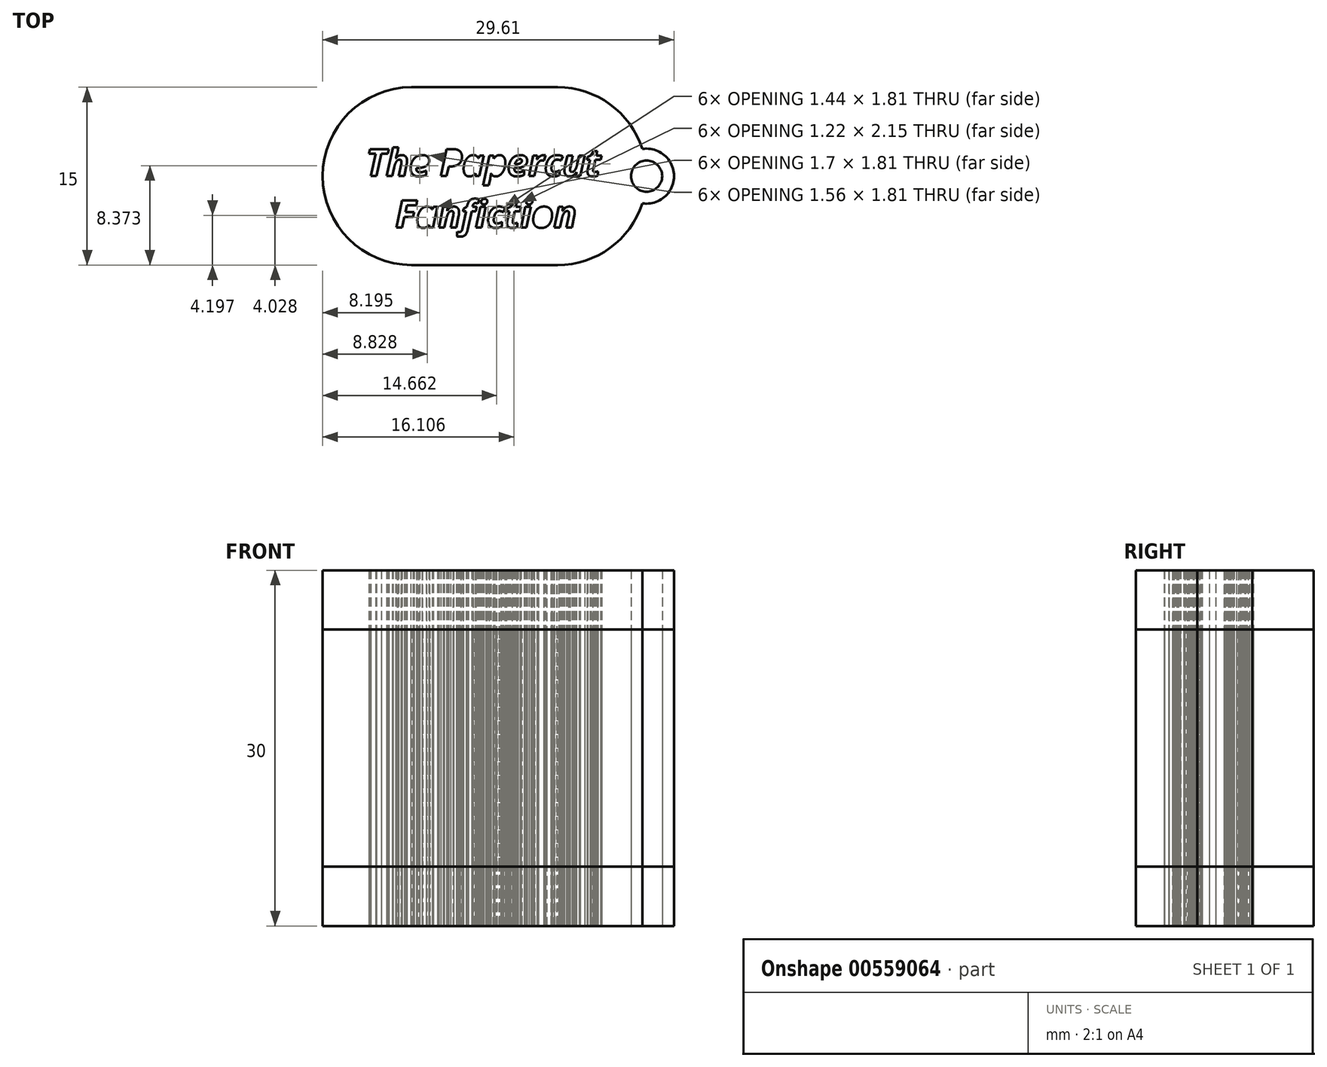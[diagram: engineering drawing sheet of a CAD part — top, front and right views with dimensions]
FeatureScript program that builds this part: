
annotation { "Feature Type Name" : "Feature", "Feature Type Description" : "" }
export const myFeature = defineFeature(function(context is Context, id is Id, definition is map)
    precondition{}
    {
        {
            var Q0;
            Q0=qCreatedBy(makeId("Top.planeOp"),FACE);
            var sketch = newSketch(context, id + "F0", { "sketchPlane" : qUnion([Q0])});
            skText(sketch, "E0", { "text": "The Papercut\n   Fanfiction", "fontName": "OpenSans-BoldItalic.ttf"});
            skLineSegment(sketch, "E1.bottom", {"start": v(6.15, 7.5) * mm, "end": v(-6.15, 7.5) * mm});
            skLineSegment(sketch, "E1.top", {"start": v(6.15, -7.5) * mm, "end": v(-6.15, -7.5) * mm});
            skLineSegment(sketch, "E1.left", {"start": v(13.65, 0) * mm, "end": v(13.65, 0) * mm});
            skLineSegment(sketch, "E1.right", {"start": v(-13.65, 0) * mm, "end": v(-13.65, 0) * mm});
            skPoint(sketch, "E1.middle", {"position": v(0, 0) * mm});
            skPoint(sketch, "E2.visualSharp", {"position": v(-13.65, 7.5) * mm});
            skArc(sketch, "E2.filletArc", {"start": v(-6.15, 7.5) * mm, "mid": v(-11.45, 5.3) * mm, "end": v(-13.65, 0) * mm});
            skPoint(sketch, "E3.visualSharp", {"position": v(-13.65, -7.5) * mm});
            skArc(sketch, "E3.filletArc", {"start": v(-13.65, 0) * mm, "mid": v(-11.45, -5.3) * mm, "end": v(-6.15, -7.5) * mm});
            skPoint(sketch, "E4.visualSharp", {"position": v(13.65, 7.5) * mm});
            skPoint(sketch, "E5.visualSharp", {"position": v(13.65, -7.5) * mm});
            skArc(sketch, "E5.filletArc", {"start": v(6.15, -7.5) * mm, "mid": v(10.57, -6.06) * mm, "end": v(13.3, -2.3) * mm});
            skLineSegment(sketch, "E6", {"start": v(13.65, 0) * mm, "end": v(13.64, 0) * mm, "construction": true});
            skArc(sketch, "E7", {"start": v(13.3, -2.3) * mm, "mid": v(15.96, 0) * mm, "end": v(13.3, 2.3) * mm});
            skPoint(sketch, "E8.end.orphan", {"position": v(12.47, 0) * mm});
            skCircle(sketch, "E9", {"center": v(13.65, 0) * mm, "radius": 1.31 * mm});
            skArc(sketch, "E10.trimOffspring", {"start": v(13.3, 2.3) * mm, "mid": v(10.57, 6.06) * mm, "end": v(6.15, 7.5) * mm});
            const initialGuessF0  = {"E0": [-0.01, 0, 1, 0, 0.0023]};
            skSetInitialGuess(sketch, initialGuessF0);
            skSolve(sketch);
        }
        {
            var Q0;
            Q0=makeQuery(id+"F0.imprint","IMPRINT",FACE,{"disambiguationData":[TD([[makeQuery(id+"F0.imprint","IMPRINT",EDGE,{"derivedFrom":sQuery(id+"F0.wireOp",EDGE,"E0.sketch_text.stroke-0")}),1.0]])]});
            extrude(context, id + "F1", {"entities" : qUnion([Q0]), "depth" : 5 * mm, "offsetDistance" : 25 * mm});
        }
        {
            var Q0;
            Q0=makeQuery(id+"F1.opExtrude","CAP_FACE",FACE,{"disambiguationData":[OSD([sQuery(id+"F0.wireOp",EDGE,"E0.sketch_text.stroke-0"),sQuery(id+"F0.wireOp",EDGE,"E0.sketch_text.stroke-1"),sQuery(id+"F0.wireOp",EDGE,"E0.sketch_text.stroke-2"),sQuery(id+"F0.wireOp",EDGE,"E0.sketch_text.stroke-3"),sQuery(id+"F0.wireOp",EDGE,"E0.sketch_text.stroke-4"),sQuery(id+"F0.wireOp",EDGE,"E0.sketch_text.stroke-5"),sQuery(id+"F0.wireOp",EDGE,"E0.sketch_text.stroke-6"),sQuery(id+"F0.wireOp",EDGE,"E0.sketch_text.stroke-7"),sQuery(id+"F0.wireOp",EDGE,"E0.sketch_text.stroke-8"),sQuery(id+"F0.wireOp",EDGE,"E0.sketch_text.stroke-9"),sQuery(id+"F0.wireOp",EDGE,"E0.sketch_text.stroke-10"),sQuery(id+"F0.wireOp",EDGE,"E0.sketch_text.stroke-11"),sQuery(id+"F0.wireOp",EDGE,"E0.sketch_text.stroke-12"),sQuery(id+"F0.wireOp",EDGE,"E0.sketch_text.stroke-13"),sQuery(id+"F0.wireOp",EDGE,"E0.sketch_text.stroke-14"),sQuery(id+"F0.wireOp",EDGE,"E0.sketch_text.stroke-15"),sQuery(id+"F0.wireOp",EDGE,"E0.sketch_text.stroke-16"),sQuery(id+"F0.wireOp",EDGE,"E0.sketch_text.stroke-17"),sQuery(id+"F0.wireOp",EDGE,"E0.sketch_text.stroke-18"),sQuery(id+"F0.wireOp",EDGE,"E0.sketch_text.stroke-19"),sQuery(id+"F0.wireOp",EDGE,"E0.sketch_text.stroke-20"),sQuery(id+"F0.wireOp",EDGE,"E0.sketch_text.stroke-21"),sQuery(id+"F0.wireOp",EDGE,"E0.sketch_text.stroke-22"),sQuery(id+"F0.wireOp",EDGE,"E0.sketch_text.stroke-23"),sQuery(id+"F0.wireOp",EDGE,"E0.sketch_text.stroke-24"),sQuery(id+"F0.wireOp",EDGE,"E0.sketch_text.stroke-25"),sQuery(id+"F0.wireOp",EDGE,"E0.sketch_text.stroke-26"),sQuery(id+"F0.wireOp",EDGE,"E0.sketch_text.stroke-33"),sQuery(id+"F0.wireOp",EDGE,"E0.sketch_text.stroke-34"),sQuery(id+"F0.wireOp",EDGE,"E0.sketch_text.stroke-35"),sQuery(id+"F0.wireOp",EDGE,"E0.sketch_text.stroke-36"),sQuery(id+"F0.wireOp",EDGE,"E0.sketch_text.stroke-37"),sQuery(id+"F0.wireOp",EDGE,"E0.sketch_text.stroke-38"),sQuery(id+"F0.wireOp",EDGE,"E0.sketch_text.stroke-39"),sQuery(id+"F0.wireOp",EDGE,"E0.sketch_text.stroke-40"),sQuery(id+"F0.wireOp",EDGE,"E0.sketch_text.stroke-41"),sQuery(id+"F0.wireOp",EDGE,"E0.sketch_text.stroke-42"),sQuery(id+"F0.wireOp",EDGE,"E0.sketch_text.stroke-43"),sQuery(id+"F0.wireOp",EDGE,"E0.sketch_text.stroke-44"),sQuery(id+"F0.wireOp",EDGE,"E0.sketch_text.stroke-45"),sQuery(id+"F0.wireOp",EDGE,"E0.sketch_text.stroke-46"),sQuery(id+"F0.wireOp",EDGE,"E0.sketch_text.stroke-47"),sQuery(id+"F0.wireOp",EDGE,"E0.sketch_text.stroke-48"),sQuery(id+"F0.wireOp",EDGE,"E0.sketch_text.stroke-49"),sQuery(id+"F0.wireOp",EDGE,"E0.sketch_text.stroke-50"),sQuery(id+"F0.wireOp",EDGE,"E0.sketch_text.stroke-57"),sQuery(id+"F0.wireOp",EDGE,"E0.sketch_text.stroke-58"),sQuery(id+"F0.wireOp",EDGE,"E0.sketch_text.stroke-59"),sQuery(id+"F0.wireOp",EDGE,"E0.sketch_text.stroke-60"),sQuery(id+"F0.wireOp",EDGE,"E0.sketch_text.stroke-61"),sQuery(id+"F0.wireOp",EDGE,"E0.sketch_text.stroke-62"),sQuery(id+"F0.wireOp",EDGE,"E0.sketch_text.stroke-63"),sQuery(id+"F0.wireOp",EDGE,"E0.sketch_text.stroke-64"),sQuery(id+"F0.wireOp",EDGE,"E0.sketch_text.stroke-65"),sQuery(id+"F0.wireOp",EDGE,"E0.sketch_text.stroke-66"),sQuery(id+"F0.wireOp",EDGE,"E0.sketch_text.stroke-67"),sQuery(id+"F0.wireOp",EDGE,"E0.sketch_text.stroke-68"),sQuery(id+"F0.wireOp",EDGE,"E0.sketch_text.stroke-69"),sQuery(id+"F0.wireOp",EDGE,"E0.sketch_text.stroke-70"),sQuery(id+"F0.wireOp",EDGE,"E0.sketch_text.stroke-71"),sQuery(id+"F0.wireOp",EDGE,"E0.sketch_text.stroke-72"),sQuery(id+"F0.wireOp",EDGE,"E0.sketch_text.stroke-73"),sQuery(id+"F0.wireOp",EDGE,"E0.sketch_text.stroke-74"),sQuery(id+"F0.wireOp",EDGE,"E0.sketch_text.stroke-75"),sQuery(id+"F0.wireOp",EDGE,"E0.sketch_text.stroke-76"),sQuery(id+"F0.wireOp",EDGE,"E0.sketch_text.stroke-77"),sQuery(id+"F0.wireOp",EDGE,"E0.sketch_text.stroke-78"),sQuery(id+"F0.wireOp",EDGE,"E0.sketch_text.stroke-79"),sQuery(id+"F0.wireOp",EDGE,"E0.sketch_text.stroke-80"),sQuery(id+"F0.wireOp",EDGE,"E0.sketch_text.stroke-91"),sQuery(id+"F0.wireOp",EDGE,"E0.sketch_text.stroke-92"),sQuery(id+"F0.wireOp",EDGE,"E0.sketch_text.stroke-93"),sQuery(id+"F0.wireOp",EDGE,"E0.sketch_text.stroke-94"),sQuery(id+"F0.wireOp",EDGE,"E0.sketch_text.stroke-95"),sQuery(id+"F0.wireOp",EDGE,"E0.sketch_text.stroke-96"),sQuery(id+"F0.wireOp",EDGE,"E0.sketch_text.stroke-97"),sQuery(id+"F0.wireOp",EDGE,"E0.sketch_text.stroke-98"),sQuery(id+"F0.wireOp",EDGE,"E0.sketch_text.stroke-99"),sQuery(id+"F0.wireOp",EDGE,"E0.sketch_text.stroke-100"),sQuery(id+"F0.wireOp",EDGE,"E0.sketch_text.stroke-101"),sQuery(id+"F0.wireOp",EDGE,"E0.sketch_text.stroke-102"),sQuery(id+"F0.wireOp",EDGE,"E0.sketch_text.stroke-103"),sQuery(id+"F0.wireOp",EDGE,"E0.sketch_text.stroke-104"),sQuery(id+"F0.wireOp",EDGE,"E0.sketch_text.stroke-105"),sQuery(id+"F0.wireOp",EDGE,"E0.sketch_text.stroke-106"),sQuery(id+"F0.wireOp",EDGE,"E0.sketch_text.stroke-122"),sQuery(id+"F0.wireOp",EDGE,"E0.sketch_text.stroke-123"),sQuery(id+"F0.wireOp",EDGE,"E0.sketch_text.stroke-124"),sQuery(id+"F0.wireOp",EDGE,"E0.sketch_text.stroke-125"),sQuery(id+"F0.wireOp",EDGE,"E0.sketch_text.stroke-126"),sQuery(id+"F0.wireOp",EDGE,"E0.sketch_text.stroke-127"),sQuery(id+"F0.wireOp",EDGE,"E0.sketch_text.stroke-128"),sQuery(id+"F0.wireOp",EDGE,"E0.sketch_text.stroke-129"),sQuery(id+"F0.wireOp",EDGE,"E0.sketch_text.stroke-130"),sQuery(id+"F0.wireOp",EDGE,"E0.sketch_text.stroke-131"),sQuery(id+"F0.wireOp",EDGE,"E0.sketch_text.stroke-132"),sQuery(id+"F0.wireOp",EDGE,"E0.sketch_text.stroke-133"),sQuery(id+"F0.wireOp",EDGE,"E0.sketch_text.stroke-134"),sQuery(id+"F0.wireOp",EDGE,"E0.sketch_text.stroke-135"),sQuery(id+"F0.wireOp",EDGE,"E0.sketch_text.stroke-136"),sQuery(id+"F0.wireOp",EDGE,"E0.sketch_text.stroke-137"),sQuery(id+"F0.wireOp",EDGE,"E0.sketch_text.stroke-138"),sQuery(id+"F0.wireOp",EDGE,"E0.sketch_text.stroke-139"),sQuery(id+"F0.wireOp",EDGE,"E0.sketch_text.stroke-140"),sQuery(id+"F0.wireOp",EDGE,"E0.sketch_text.stroke-141"),sQuery(id+"F0.wireOp",EDGE,"E0.sketch_text.stroke-142"),sQuery(id+"F0.wireOp",EDGE,"E0.sketch_text.stroke-143"),sQuery(id+"F0.wireOp",EDGE,"E0.sketch_text.stroke-144"),sQuery(id+"F0.wireOp",EDGE,"E0.sketch_text.stroke-145"),sQuery(id+"F0.wireOp",EDGE,"E0.sketch_text.stroke-146"),sQuery(id+"F0.wireOp",EDGE,"E0.sketch_text.stroke-147"),sQuery(id+"F0.wireOp",EDGE,"E0.sketch_text.stroke-148"),sQuery(id+"F0.wireOp",EDGE,"E0.sketch_text.stroke-149"),sQuery(id+"F0.wireOp",EDGE,"E0.sketch_text.stroke-150"),sQuery(id+"F0.wireOp",EDGE,"E0.sketch_text.stroke-151"),sQuery(id+"F0.wireOp",EDGE,"E0.sketch_text.stroke-152"),sQuery(id+"F0.wireOp",EDGE,"E0.sketch_text.stroke-153"),sQuery(id+"F0.wireOp",EDGE,"E0.sketch_text.stroke-154"),sQuery(id+"F0.wireOp",EDGE,"E0.sketch_text.stroke-155"),sQuery(id+"F0.wireOp",EDGE,"E0.sketch_text.stroke-156"),sQuery(id+"F0.wireOp",EDGE,"E0.sketch_text.stroke-157"),sQuery(id+"F0.wireOp",EDGE,"E0.sketch_text.stroke-158"),sQuery(id+"F0.wireOp",EDGE,"E0.sketch_text.stroke-159"),sQuery(id+"F0.wireOp",EDGE,"E0.sketch_text.stroke-160"),sQuery(id+"F0.wireOp",EDGE,"E0.sketch_text.stroke-161"),sQuery(id+"F0.wireOp",EDGE,"E0.sketch_text.stroke-162"),sQuery(id+"F0.wireOp",EDGE,"E0.sketch_text.stroke-163"),sQuery(id+"F0.wireOp",EDGE,"E0.sketch_text.stroke-164"),sQuery(id+"F0.wireOp",EDGE,"E0.sketch_text.stroke-165"),sQuery(id+"F0.wireOp",EDGE,"E0.sketch_text.stroke-166"),sQuery(id+"F0.wireOp",EDGE,"E0.sketch_text.stroke-167"),sQuery(id+"F0.wireOp",EDGE,"E0.sketch_text.stroke-168"),sQuery(id+"F0.wireOp",EDGE,"E0.sketch_text.stroke-169"),sQuery(id+"F0.wireOp",EDGE,"E0.sketch_text.stroke-170"),sQuery(id+"F0.wireOp",EDGE,"E0.sketch_text.stroke-171"),sQuery(id+"F0.wireOp",EDGE,"E0.sketch_text.stroke-172"),sQuery(id+"F0.wireOp",EDGE,"E0.sketch_text.stroke-173"),sQuery(id+"F0.wireOp",EDGE,"E0.sketch_text.stroke-174"),sQuery(id+"F0.wireOp",EDGE,"E0.sketch_text.stroke-175"),sQuery(id+"F0.wireOp",EDGE,"E0.sketch_text.stroke-176"),sQuery(id+"F0.wireOp",EDGE,"E0.sketch_text.stroke-177"),sQuery(id+"F0.wireOp",EDGE,"E0.sketch_text.stroke-178"),sQuery(id+"F0.wireOp",EDGE,"E0.sketch_text.stroke-179"),sQuery(id+"F0.wireOp",EDGE,"E0.sketch_text.stroke-180"),sQuery(id+"F0.wireOp",EDGE,"E0.sketch_text.stroke-181"),sQuery(id+"F0.wireOp",EDGE,"E0.sketch_text.stroke-182"),sQuery(id+"F0.wireOp",EDGE,"E0.sketch_text.stroke-183"),sQuery(id+"F0.wireOp",EDGE,"E0.sketch_text.stroke-184"),sQuery(id+"F0.wireOp",EDGE,"E0.sketch_text.stroke-185"),sQuery(id+"F0.wireOp",EDGE,"E0.sketch_text.stroke-186"),sQuery(id+"F0.wireOp",EDGE,"E0.sketch_text.stroke-187"),sQuery(id+"F0.wireOp",EDGE,"E0.sketch_text.stroke-188"),sQuery(id+"F0.wireOp",EDGE,"E0.sketch_text.stroke-189"),sQuery(id+"F0.wireOp",EDGE,"E0.sketch_text.stroke-190"),sQuery(id+"F0.wireOp",EDGE,"E0.sketch_text.stroke-191"),sQuery(id+"F0.wireOp",EDGE,"E0.sketch_text.stroke-192"),sQuery(id+"F0.wireOp",EDGE,"E0.sketch_text.stroke-193"),sQuery(id+"F0.wireOp",EDGE,"E0.sketch_text.stroke-194"),sQuery(id+"F0.wireOp",EDGE,"E0.sketch_text.stroke-195"),sQuery(id+"F0.wireOp",EDGE,"E0.sketch_text.stroke-196"),sQuery(id+"F0.wireOp",EDGE,"E0.sketch_text.stroke-197"),sQuery(id+"F0.wireOp",EDGE,"E0.sketch_text.stroke-198"),sQuery(id+"F0.wireOp",EDGE,"E0.sketch_text.stroke-199"),sQuery(id+"F0.wireOp",EDGE,"E0.sketch_text.stroke-200"),sQuery(id+"F0.wireOp",EDGE,"E0.sketch_text.stroke-201"),sQuery(id+"F0.wireOp",EDGE,"E0.sketch_text.stroke-202"),sQuery(id+"F0.wireOp",EDGE,"E0.sketch_text.stroke-203"),sQuery(id+"F0.wireOp",EDGE,"E0.sketch_text.stroke-204"),sQuery(id+"F0.wireOp",EDGE,"E0.sketch_text.stroke-205"),sQuery(id+"F0.wireOp",EDGE,"E0.sketch_text.stroke-206"),sQuery(id+"F0.wireOp",EDGE,"E0.sketch_text.stroke-207"),sQuery(id+"F0.wireOp",EDGE,"E0.sketch_text.stroke-208"),sQuery(id+"F0.wireOp",EDGE,"E0.sketch_text.stroke-209"),sQuery(id+"F0.wireOp",EDGE,"E0.sketch_text.stroke-210"),sQuery(id+"F0.wireOp",EDGE,"E0.sketch_text.stroke-211"),sQuery(id+"F0.wireOp",EDGE,"E0.sketch_text.stroke-212"),sQuery(id+"F0.wireOp",EDGE,"E0.sketch_text.stroke-213"),sQuery(id+"F0.wireOp",EDGE,"E0.sketch_text.stroke-214"),sQuery(id+"F0.wireOp",EDGE,"E0.sketch_text.stroke-215"),sQuery(id+"F0.wireOp",EDGE,"E0.sketch_text.stroke-216"),sQuery(id+"F0.wireOp",EDGE,"E0.sketch_text.stroke-217"),sQuery(id+"F0.wireOp",EDGE,"E0.sketch_text.stroke-218"),sQuery(id+"F0.wireOp",EDGE,"E0.sketch_text.stroke-219"),sQuery(id+"F0.wireOp",EDGE,"E0.sketch_text.stroke-220"),sQuery(id+"F0.wireOp",EDGE,"E0.sketch_text.stroke-221"),sQuery(id+"F0.wireOp",EDGE,"E0.sketch_text.stroke-222"),sQuery(id+"F0.wireOp",EDGE,"E0.sketch_text.stroke-223"),sQuery(id+"F0.wireOp",EDGE,"E0.sketch_text.stroke-224"),sQuery(id+"F0.wireOp",EDGE,"E0.sketch_text.stroke-225"),sQuery(id+"F0.wireOp",EDGE,"E0.sketch_text.stroke-226"),sQuery(id+"F0.wireOp",EDGE,"E0.sketch_text.stroke-227"),sQuery(id+"F0.wireOp",EDGE,"E0.sketch_text.stroke-228"),sQuery(id+"F0.wireOp",EDGE,"E0.sketch_text.stroke-229"),sQuery(id+"F0.wireOp",EDGE,"E0.sketch_text.stroke-230"),sQuery(id+"F0.wireOp",EDGE,"E0.sketch_text.stroke-241"),sQuery(id+"F0.wireOp",EDGE,"E0.sketch_text.stroke-242"),sQuery(id+"F0.wireOp",EDGE,"E0.sketch_text.stroke-243"),sQuery(id+"F0.wireOp",EDGE,"E0.sketch_text.stroke-244"),sQuery(id+"F0.wireOp",EDGE,"E0.sketch_text.stroke-245"),sQuery(id+"F0.wireOp",EDGE,"E0.sketch_text.stroke-246"),sQuery(id+"F0.wireOp",EDGE,"E0.sketch_text.stroke-247"),sQuery(id+"F0.wireOp",EDGE,"E0.sketch_text.stroke-248"),sQuery(id+"F0.wireOp",EDGE,"E0.sketch_text.stroke-249"),sQuery(id+"F0.wireOp",EDGE,"E0.sketch_text.stroke-250"),sQuery(id+"F0.wireOp",EDGE,"E0.sketch_text.stroke-251"),sQuery(id+"F0.wireOp",EDGE,"E0.sketch_text.stroke-252"),sQuery(id+"F0.wireOp",EDGE,"E0.sketch_text.stroke-253"),sQuery(id+"F0.wireOp",EDGE,"E0.sketch_text.stroke-254"),sQuery(id+"F0.wireOp",EDGE,"E0.sketch_text.stroke-255"),sQuery(id+"F0.wireOp",EDGE,"E0.sketch_text.stroke-256"),sQuery(id+"F0.wireOp",EDGE,"E0.sketch_text.stroke-257"),sQuery(id+"F0.wireOp",EDGE,"E0.sketch_text.stroke-258"),sQuery(id+"F0.wireOp",EDGE,"E0.sketch_text.stroke-259"),sQuery(id+"F0.wireOp",EDGE,"E0.sketch_text.stroke-260"),sQuery(id+"F0.wireOp",EDGE,"E0.sketch_text.stroke-261"),sQuery(id+"F0.wireOp",EDGE,"E0.sketch_text.stroke-262"),sQuery(id+"F0.wireOp",EDGE,"E0.sketch_text.stroke-263"),sQuery(id+"F0.wireOp",EDGE,"E0.sketch_text.stroke-264"),sQuery(id+"F0.wireOp",EDGE,"E0.sketch_text.stroke-265"),sQuery(id+"F0.wireOp",EDGE,"E0.sketch_text.stroke-266"),sQuery(id+"F0.wireOp",EDGE,"E0.sketch_text.stroke-267"),sQuery(id+"F0.wireOp",EDGE,"E0.sketch_text.stroke-268"),sQuery(id+"F0.wireOp",EDGE,"E0.sketch_text.stroke-269"),sQuery(id+"F0.wireOp",EDGE,"E0.sketch_text.stroke-270"),sQuery(id+"F0.wireOp",EDGE,"E0.sketch_text.stroke-271"),sQuery(id+"F0.wireOp",EDGE,"E0.sketch_text.stroke-272"),sQuery(id+"F0.wireOp",EDGE,"E0.sketch_text.stroke-273"),sQuery(id+"F0.wireOp",EDGE,"E0.sketch_text.stroke-274"),sQuery(id+"F0.wireOp",EDGE,"E0.sketch_text.stroke-275"),sQuery(id+"F0.wireOp",EDGE,"E0.sketch_text.stroke-276"),sQuery(id+"F0.wireOp",EDGE,"E0.sketch_text.stroke-277"),sQuery(id+"F0.wireOp",EDGE,"E0.sketch_text.stroke-278"),sQuery(id+"F0.wireOp",EDGE,"E0.sketch_text.stroke-279"),sQuery(id+"F0.wireOp",EDGE,"E0.sketch_text.stroke-280"),sQuery(id+"F0.wireOp",EDGE,"E0.sketch_text.stroke-281"),sQuery(id+"F0.wireOp",EDGE,"E0.sketch_text.stroke-282"),sQuery(id+"F0.wireOp",EDGE,"E0.sketch_text.stroke-283"),sQuery(id+"F0.wireOp",EDGE,"E0.sketch_text.stroke-284"),sQuery(id+"F0.wireOp",EDGE,"E0.sketch_text.stroke-285"),sQuery(id+"F0.wireOp",EDGE,"E0.sketch_text.stroke-286"),sQuery(id+"F0.wireOp",EDGE,"E0.sketch_text.stroke-287"),sQuery(id+"F0.wireOp",EDGE,"E0.sketch_text.stroke-288"),sQuery(id+"F0.wireOp",EDGE,"E0.sketch_text.stroke-289"),sQuery(id+"F0.wireOp",EDGE,"E0.sketch_text.stroke-290"),sQuery(id+"F0.wireOp",EDGE,"E0.sketch_text.stroke-291"),sQuery(id+"F0.wireOp",EDGE,"E0.sketch_text.stroke-292"),sQuery(id+"F0.wireOp",EDGE,"E0.sketch_text.stroke-293"),sQuery(id+"F0.wireOp",EDGE,"E0.sketch_text.stroke-294"),sQuery(id+"F0.wireOp",EDGE,"E0.sketch_text.stroke-295"),sQuery(id+"F0.wireOp",EDGE,"E0.sketch_text.stroke-296"),sQuery(id+"F0.wireOp",EDGE,"E0.sketch_text.stroke-297"),sQuery(id+"F0.wireOp",EDGE,"E0.sketch_text.stroke-298"),sQuery(id+"F0.wireOp",EDGE,"E0.sketch_text.stroke-299"),sQuery(id+"F0.wireOp",EDGE,"E0.sketch_text.stroke-300"),sQuery(id+"F0.wireOp",EDGE,"E0.sketch_text.stroke-301"),sQuery(id+"F0.wireOp",EDGE,"E0.sketch_text.stroke-302"),sQuery(id+"F0.wireOp",EDGE,"E0.sketch_text.stroke-303"),sQuery(id+"F0.wireOp",EDGE,"E0.sketch_text.stroke-304"),sQuery(id+"F0.wireOp",EDGE,"E0.sketch_text.stroke-305"),sQuery(id+"F0.wireOp",EDGE,"E0.sketch_text.stroke-306"),sQuery(id+"F0.wireOp",EDGE,"E0.sketch_text.stroke-307"),sQuery(id+"F0.wireOp",EDGE,"E0.sketch_text.stroke-308"),sQuery(id+"F0.wireOp",EDGE,"E0.sketch_text.stroke-309"),sQuery(id+"F0.wireOp",EDGE,"E0.sketch_text.stroke-310"),sQuery(id+"F0.wireOp",EDGE,"E0.sketch_text.stroke-311"),sQuery(id+"F0.wireOp",EDGE,"E0.sketch_text.stroke-312"),sQuery(id+"F0.wireOp",EDGE,"E0.sketch_text.stroke-313"),sQuery(id+"F0.wireOp",EDGE,"E0.sketch_text.stroke-314"),sQuery(id+"F0.wireOp",EDGE,"E0.sketch_text.stroke-315"),sQuery(id+"F0.wireOp",EDGE,"E0.sketch_text.stroke-316"),sQuery(id+"F0.wireOp",EDGE,"E0.sketch_text.stroke-317"),sQuery(id+"F0.wireOp",EDGE,"E0.sketch_text.stroke-318"),sQuery(id+"F0.wireOp",EDGE,"E0.sketch_text.stroke-319"),sQuery(id+"F0.wireOp",EDGE,"E0.sketch_text.stroke-320"),sQuery(id+"F0.wireOp",EDGE,"E0.sketch_text.stroke-321"),sQuery(id+"F0.wireOp",EDGE,"E0.sketch_text.stroke-322"),sQuery(id+"F0.wireOp",EDGE,"E0.sketch_text.stroke-323"),sQuery(id+"F0.wireOp",EDGE,"E0.sketch_text.stroke-324"),sQuery(id+"F0.wireOp",EDGE,"E0.sketch_text.stroke-325"),sQuery(id+"F0.wireOp",EDGE,"E0.sketch_text.stroke-326"),sQuery(id+"F0.wireOp",EDGE,"E0.sketch_text.stroke-327"),sQuery(id+"F0.wireOp",EDGE,"E0.sketch_text.stroke-328"),sQuery(id+"F0.wireOp",EDGE,"E0.sketch_text.stroke-329"),sQuery(id+"F0.wireOp",EDGE,"E0.sketch_text.stroke-330"),sQuery(id+"F0.wireOp",EDGE,"E0.sketch_text.stroke-331"),sQuery(id+"F0.wireOp",EDGE,"E0.sketch_text.stroke-332"),sQuery(id+"F0.wireOp",EDGE,"E0.sketch_text.stroke-333"),sQuery(id+"F0.wireOp",EDGE,"E0.sketch_text.stroke-334"),sQuery(id+"F0.wireOp",EDGE,"E0.sketch_text.stroke-335"),sQuery(id+"F0.wireOp",EDGE,"E0.sketch_text.stroke-336"),sQuery(id+"F0.wireOp",EDGE,"E0.sketch_text.stroke-337"),sQuery(id+"F0.wireOp",EDGE,"E0.sketch_text.stroke-338"),sQuery(id+"F0.wireOp",EDGE,"E0.sketch_text.stroke-339"),sQuery(id+"F0.wireOp",EDGE,"E0.sketch_text.stroke-348"),sQuery(id+"F0.wireOp",EDGE,"E0.sketch_text.stroke-349"),sQuery(id+"F0.wireOp",EDGE,"E0.sketch_text.stroke-350"),sQuery(id+"F0.wireOp",EDGE,"E0.sketch_text.stroke-351"),sQuery(id+"F0.wireOp",EDGE,"E0.sketch_text.stroke-352"),sQuery(id+"F0.wireOp",EDGE,"E0.sketch_text.stroke-353"),sQuery(id+"F0.wireOp",EDGE,"E0.sketch_text.stroke-354"),sQuery(id+"F0.wireOp",EDGE,"E0.sketch_text.stroke-355"),sQuery(id+"F0.wireOp",EDGE,"E0.sketch_text.stroke-356"),sQuery(id+"F0.wireOp",EDGE,"E0.sketch_text.stroke-357"),sQuery(id+"F0.wireOp",EDGE,"E0.sketch_text.stroke-358"),sQuery(id+"F0.wireOp",EDGE,"E0.sketch_text.stroke-359"),sQuery(id+"F0.wireOp",EDGE,"E0.sketch_text.stroke-360"),sQuery(id+"F0.wireOp",EDGE,"E0.sketch_text.stroke-361"),sQuery(id+"F0.wireOp",EDGE,"E0.sketch_text.stroke-362"),sQuery(id+"F0.wireOp",EDGE,"E0.sketch_text.stroke-363"),sQuery(id+"F0.wireOp",EDGE,"E0.sketch_text.stroke-364"),sQuery(id+"F0.wireOp",EDGE,"E0.sketch_text.stroke-365"),sQuery(id+"F0.wireOp",EDGE,"E0.sketch_text.stroke-366"),sQuery(id+"F0.wireOp",EDGE,"E0.sketch_text.stroke-367"),sQuery(id+"F0.wireOp",EDGE,"E0.sketch_text.stroke-368"),sQuery(id+"F0.wireOp",EDGE,"E0.sketch_text.stroke-369"),sQuery(id+"F0.wireOp",EDGE,"E0.sketch_text.stroke-370"),sQuery(id+"F0.wireOp",EDGE,"E0.sketch_text.stroke-371"),sQuery(id+"F0.wireOp",EDGE,"E0.sketch_text.stroke-372"),sQuery(id+"F0.wireOp",EDGE,"E0.sketch_text.stroke-373"),sQuery(id+"F0.wireOp",EDGE,"E0.sketch_text.stroke-374"),sQuery(id+"F0.wireOp",EDGE,"E1.bottom"),sQuery(id+"F0.wireOp",EDGE,"E1.top"),sQuery(id+"F0.wireOp",EDGE,"E2.filletArc"),sQuery(id+"F0.wireOp",EDGE,"E3.filletArc"),sQuery(id+"F0.wireOp",EDGE,"E5.filletArc"),sQuery(id+"F0.wireOp",EDGE,"E7"),sQuery(id+"F0.wireOp",EDGE,"E9"),sQuery(id+"F0.wireOp",EDGE,"E10.trimOffspring")])],"isStart":false});
            var Q1;
            Q1=makeQuery(id+"F1.opExtrude","CAP_FACE",FACE,{"disambiguationData":[OSD([sQuery(id+"F0.wireOp",EDGE,"E0.sketch_text.stroke-0"),sQuery(id+"F0.wireOp",EDGE,"E0.sketch_text.stroke-1"),sQuery(id+"F0.wireOp",EDGE,"E0.sketch_text.stroke-2"),sQuery(id+"F0.wireOp",EDGE,"E0.sketch_text.stroke-3"),sQuery(id+"F0.wireOp",EDGE,"E0.sketch_text.stroke-4"),sQuery(id+"F0.wireOp",EDGE,"E0.sketch_text.stroke-5"),sQuery(id+"F0.wireOp",EDGE,"E0.sketch_text.stroke-6"),sQuery(id+"F0.wireOp",EDGE,"E0.sketch_text.stroke-7"),sQuery(id+"F0.wireOp",EDGE,"E0.sketch_text.stroke-8"),sQuery(id+"F0.wireOp",EDGE,"E0.sketch_text.stroke-9"),sQuery(id+"F0.wireOp",EDGE,"E0.sketch_text.stroke-10"),sQuery(id+"F0.wireOp",EDGE,"E0.sketch_text.stroke-11"),sQuery(id+"F0.wireOp",EDGE,"E0.sketch_text.stroke-12"),sQuery(id+"F0.wireOp",EDGE,"E0.sketch_text.stroke-13"),sQuery(id+"F0.wireOp",EDGE,"E0.sketch_text.stroke-14"),sQuery(id+"F0.wireOp",EDGE,"E0.sketch_text.stroke-15"),sQuery(id+"F0.wireOp",EDGE,"E0.sketch_text.stroke-16"),sQuery(id+"F0.wireOp",EDGE,"E0.sketch_text.stroke-17"),sQuery(id+"F0.wireOp",EDGE,"E0.sketch_text.stroke-18"),sQuery(id+"F0.wireOp",EDGE,"E0.sketch_text.stroke-19"),sQuery(id+"F0.wireOp",EDGE,"E0.sketch_text.stroke-20"),sQuery(id+"F0.wireOp",EDGE,"E0.sketch_text.stroke-21"),sQuery(id+"F0.wireOp",EDGE,"E0.sketch_text.stroke-22"),sQuery(id+"F0.wireOp",EDGE,"E0.sketch_text.stroke-23"),sQuery(id+"F0.wireOp",EDGE,"E0.sketch_text.stroke-24"),sQuery(id+"F0.wireOp",EDGE,"E0.sketch_text.stroke-25"),sQuery(id+"F0.wireOp",EDGE,"E0.sketch_text.stroke-26"),sQuery(id+"F0.wireOp",EDGE,"E0.sketch_text.stroke-33"),sQuery(id+"F0.wireOp",EDGE,"E0.sketch_text.stroke-34"),sQuery(id+"F0.wireOp",EDGE,"E0.sketch_text.stroke-35"),sQuery(id+"F0.wireOp",EDGE,"E0.sketch_text.stroke-36"),sQuery(id+"F0.wireOp",EDGE,"E0.sketch_text.stroke-37"),sQuery(id+"F0.wireOp",EDGE,"E0.sketch_text.stroke-38"),sQuery(id+"F0.wireOp",EDGE,"E0.sketch_text.stroke-39"),sQuery(id+"F0.wireOp",EDGE,"E0.sketch_text.stroke-40"),sQuery(id+"F0.wireOp",EDGE,"E0.sketch_text.stroke-41"),sQuery(id+"F0.wireOp",EDGE,"E0.sketch_text.stroke-42"),sQuery(id+"F0.wireOp",EDGE,"E0.sketch_text.stroke-43"),sQuery(id+"F0.wireOp",EDGE,"E0.sketch_text.stroke-44"),sQuery(id+"F0.wireOp",EDGE,"E0.sketch_text.stroke-45"),sQuery(id+"F0.wireOp",EDGE,"E0.sketch_text.stroke-46"),sQuery(id+"F0.wireOp",EDGE,"E0.sketch_text.stroke-47"),sQuery(id+"F0.wireOp",EDGE,"E0.sketch_text.stroke-48"),sQuery(id+"F0.wireOp",EDGE,"E0.sketch_text.stroke-49"),sQuery(id+"F0.wireOp",EDGE,"E0.sketch_text.stroke-50"),sQuery(id+"F0.wireOp",EDGE,"E0.sketch_text.stroke-57"),sQuery(id+"F0.wireOp",EDGE,"E0.sketch_text.stroke-58"),sQuery(id+"F0.wireOp",EDGE,"E0.sketch_text.stroke-59"),sQuery(id+"F0.wireOp",EDGE,"E0.sketch_text.stroke-60"),sQuery(id+"F0.wireOp",EDGE,"E0.sketch_text.stroke-61"),sQuery(id+"F0.wireOp",EDGE,"E0.sketch_text.stroke-62"),sQuery(id+"F0.wireOp",EDGE,"E0.sketch_text.stroke-63"),sQuery(id+"F0.wireOp",EDGE,"E0.sketch_text.stroke-64"),sQuery(id+"F0.wireOp",EDGE,"E0.sketch_text.stroke-65"),sQuery(id+"F0.wireOp",EDGE,"E0.sketch_text.stroke-66"),sQuery(id+"F0.wireOp",EDGE,"E0.sketch_text.stroke-67"),sQuery(id+"F0.wireOp",EDGE,"E0.sketch_text.stroke-68"),sQuery(id+"F0.wireOp",EDGE,"E0.sketch_text.stroke-69"),sQuery(id+"F0.wireOp",EDGE,"E0.sketch_text.stroke-70"),sQuery(id+"F0.wireOp",EDGE,"E0.sketch_text.stroke-71"),sQuery(id+"F0.wireOp",EDGE,"E0.sketch_text.stroke-72"),sQuery(id+"F0.wireOp",EDGE,"E0.sketch_text.stroke-73"),sQuery(id+"F0.wireOp",EDGE,"E0.sketch_text.stroke-74"),sQuery(id+"F0.wireOp",EDGE,"E0.sketch_text.stroke-75"),sQuery(id+"F0.wireOp",EDGE,"E0.sketch_text.stroke-76"),sQuery(id+"F0.wireOp",EDGE,"E0.sketch_text.stroke-77"),sQuery(id+"F0.wireOp",EDGE,"E0.sketch_text.stroke-78"),sQuery(id+"F0.wireOp",EDGE,"E0.sketch_text.stroke-79"),sQuery(id+"F0.wireOp",EDGE,"E0.sketch_text.stroke-80"),sQuery(id+"F0.wireOp",EDGE,"E0.sketch_text.stroke-91"),sQuery(id+"F0.wireOp",EDGE,"E0.sketch_text.stroke-92"),sQuery(id+"F0.wireOp",EDGE,"E0.sketch_text.stroke-93"),sQuery(id+"F0.wireOp",EDGE,"E0.sketch_text.stroke-94"),sQuery(id+"F0.wireOp",EDGE,"E0.sketch_text.stroke-95"),sQuery(id+"F0.wireOp",EDGE,"E0.sketch_text.stroke-96"),sQuery(id+"F0.wireOp",EDGE,"E0.sketch_text.stroke-97"),sQuery(id+"F0.wireOp",EDGE,"E0.sketch_text.stroke-98"),sQuery(id+"F0.wireOp",EDGE,"E0.sketch_text.stroke-99"),sQuery(id+"F0.wireOp",EDGE,"E0.sketch_text.stroke-100"),sQuery(id+"F0.wireOp",EDGE,"E0.sketch_text.stroke-101"),sQuery(id+"F0.wireOp",EDGE,"E0.sketch_text.stroke-102"),sQuery(id+"F0.wireOp",EDGE,"E0.sketch_text.stroke-103"),sQuery(id+"F0.wireOp",EDGE,"E0.sketch_text.stroke-104"),sQuery(id+"F0.wireOp",EDGE,"E0.sketch_text.stroke-105"),sQuery(id+"F0.wireOp",EDGE,"E0.sketch_text.stroke-106"),sQuery(id+"F0.wireOp",EDGE,"E0.sketch_text.stroke-122"),sQuery(id+"F0.wireOp",EDGE,"E0.sketch_text.stroke-123"),sQuery(id+"F0.wireOp",EDGE,"E0.sketch_text.stroke-124"),sQuery(id+"F0.wireOp",EDGE,"E0.sketch_text.stroke-125"),sQuery(id+"F0.wireOp",EDGE,"E0.sketch_text.stroke-126"),sQuery(id+"F0.wireOp",EDGE,"E0.sketch_text.stroke-127"),sQuery(id+"F0.wireOp",EDGE,"E0.sketch_text.stroke-128"),sQuery(id+"F0.wireOp",EDGE,"E0.sketch_text.stroke-129"),sQuery(id+"F0.wireOp",EDGE,"E0.sketch_text.stroke-130"),sQuery(id+"F0.wireOp",EDGE,"E0.sketch_text.stroke-131"),sQuery(id+"F0.wireOp",EDGE,"E0.sketch_text.stroke-132"),sQuery(id+"F0.wireOp",EDGE,"E0.sketch_text.stroke-133"),sQuery(id+"F0.wireOp",EDGE,"E0.sketch_text.stroke-134"),sQuery(id+"F0.wireOp",EDGE,"E0.sketch_text.stroke-135"),sQuery(id+"F0.wireOp",EDGE,"E0.sketch_text.stroke-136"),sQuery(id+"F0.wireOp",EDGE,"E0.sketch_text.stroke-137"),sQuery(id+"F0.wireOp",EDGE,"E0.sketch_text.stroke-138"),sQuery(id+"F0.wireOp",EDGE,"E0.sketch_text.stroke-139"),sQuery(id+"F0.wireOp",EDGE,"E0.sketch_text.stroke-140"),sQuery(id+"F0.wireOp",EDGE,"E0.sketch_text.stroke-141"),sQuery(id+"F0.wireOp",EDGE,"E0.sketch_text.stroke-142"),sQuery(id+"F0.wireOp",EDGE,"E0.sketch_text.stroke-143"),sQuery(id+"F0.wireOp",EDGE,"E0.sketch_text.stroke-144"),sQuery(id+"F0.wireOp",EDGE,"E0.sketch_text.stroke-145"),sQuery(id+"F0.wireOp",EDGE,"E0.sketch_text.stroke-146"),sQuery(id+"F0.wireOp",EDGE,"E0.sketch_text.stroke-147"),sQuery(id+"F0.wireOp",EDGE,"E0.sketch_text.stroke-148"),sQuery(id+"F0.wireOp",EDGE,"E0.sketch_text.stroke-149"),sQuery(id+"F0.wireOp",EDGE,"E0.sketch_text.stroke-150"),sQuery(id+"F0.wireOp",EDGE,"E0.sketch_text.stroke-151"),sQuery(id+"F0.wireOp",EDGE,"E0.sketch_text.stroke-152"),sQuery(id+"F0.wireOp",EDGE,"E0.sketch_text.stroke-153"),sQuery(id+"F0.wireOp",EDGE,"E0.sketch_text.stroke-154"),sQuery(id+"F0.wireOp",EDGE,"E0.sketch_text.stroke-155"),sQuery(id+"F0.wireOp",EDGE,"E0.sketch_text.stroke-156"),sQuery(id+"F0.wireOp",EDGE,"E0.sketch_text.stroke-157"),sQuery(id+"F0.wireOp",EDGE,"E0.sketch_text.stroke-158"),sQuery(id+"F0.wireOp",EDGE,"E0.sketch_text.stroke-159"),sQuery(id+"F0.wireOp",EDGE,"E0.sketch_text.stroke-160"),sQuery(id+"F0.wireOp",EDGE,"E0.sketch_text.stroke-161"),sQuery(id+"F0.wireOp",EDGE,"E0.sketch_text.stroke-162"),sQuery(id+"F0.wireOp",EDGE,"E0.sketch_text.stroke-163"),sQuery(id+"F0.wireOp",EDGE,"E0.sketch_text.stroke-164"),sQuery(id+"F0.wireOp",EDGE,"E0.sketch_text.stroke-165"),sQuery(id+"F0.wireOp",EDGE,"E0.sketch_text.stroke-166"),sQuery(id+"F0.wireOp",EDGE,"E0.sketch_text.stroke-167"),sQuery(id+"F0.wireOp",EDGE,"E0.sketch_text.stroke-168"),sQuery(id+"F0.wireOp",EDGE,"E0.sketch_text.stroke-169"),sQuery(id+"F0.wireOp",EDGE,"E0.sketch_text.stroke-170"),sQuery(id+"F0.wireOp",EDGE,"E0.sketch_text.stroke-171"),sQuery(id+"F0.wireOp",EDGE,"E0.sketch_text.stroke-172"),sQuery(id+"F0.wireOp",EDGE,"E0.sketch_text.stroke-173"),sQuery(id+"F0.wireOp",EDGE,"E0.sketch_text.stroke-174"),sQuery(id+"F0.wireOp",EDGE,"E0.sketch_text.stroke-175"),sQuery(id+"F0.wireOp",EDGE,"E0.sketch_text.stroke-176"),sQuery(id+"F0.wireOp",EDGE,"E0.sketch_text.stroke-177"),sQuery(id+"F0.wireOp",EDGE,"E0.sketch_text.stroke-178"),sQuery(id+"F0.wireOp",EDGE,"E0.sketch_text.stroke-179"),sQuery(id+"F0.wireOp",EDGE,"E0.sketch_text.stroke-180"),sQuery(id+"F0.wireOp",EDGE,"E0.sketch_text.stroke-181"),sQuery(id+"F0.wireOp",EDGE,"E0.sketch_text.stroke-182"),sQuery(id+"F0.wireOp",EDGE,"E0.sketch_text.stroke-183"),sQuery(id+"F0.wireOp",EDGE,"E0.sketch_text.stroke-184"),sQuery(id+"F0.wireOp",EDGE,"E0.sketch_text.stroke-185"),sQuery(id+"F0.wireOp",EDGE,"E0.sketch_text.stroke-186"),sQuery(id+"F0.wireOp",EDGE,"E0.sketch_text.stroke-187"),sQuery(id+"F0.wireOp",EDGE,"E0.sketch_text.stroke-188"),sQuery(id+"F0.wireOp",EDGE,"E0.sketch_text.stroke-189"),sQuery(id+"F0.wireOp",EDGE,"E0.sketch_text.stroke-190"),sQuery(id+"F0.wireOp",EDGE,"E0.sketch_text.stroke-191"),sQuery(id+"F0.wireOp",EDGE,"E0.sketch_text.stroke-192"),sQuery(id+"F0.wireOp",EDGE,"E0.sketch_text.stroke-193"),sQuery(id+"F0.wireOp",EDGE,"E0.sketch_text.stroke-194"),sQuery(id+"F0.wireOp",EDGE,"E0.sketch_text.stroke-195"),sQuery(id+"F0.wireOp",EDGE,"E0.sketch_text.stroke-196"),sQuery(id+"F0.wireOp",EDGE,"E0.sketch_text.stroke-197"),sQuery(id+"F0.wireOp",EDGE,"E0.sketch_text.stroke-198"),sQuery(id+"F0.wireOp",EDGE,"E0.sketch_text.stroke-199"),sQuery(id+"F0.wireOp",EDGE,"E0.sketch_text.stroke-200"),sQuery(id+"F0.wireOp",EDGE,"E0.sketch_text.stroke-201"),sQuery(id+"F0.wireOp",EDGE,"E0.sketch_text.stroke-202"),sQuery(id+"F0.wireOp",EDGE,"E0.sketch_text.stroke-203"),sQuery(id+"F0.wireOp",EDGE,"E0.sketch_text.stroke-204"),sQuery(id+"F0.wireOp",EDGE,"E0.sketch_text.stroke-205"),sQuery(id+"F0.wireOp",EDGE,"E0.sketch_text.stroke-206"),sQuery(id+"F0.wireOp",EDGE,"E0.sketch_text.stroke-207"),sQuery(id+"F0.wireOp",EDGE,"E0.sketch_text.stroke-208"),sQuery(id+"F0.wireOp",EDGE,"E0.sketch_text.stroke-209"),sQuery(id+"F0.wireOp",EDGE,"E0.sketch_text.stroke-210"),sQuery(id+"F0.wireOp",EDGE,"E0.sketch_text.stroke-211"),sQuery(id+"F0.wireOp",EDGE,"E0.sketch_text.stroke-212"),sQuery(id+"F0.wireOp",EDGE,"E0.sketch_text.stroke-213"),sQuery(id+"F0.wireOp",EDGE,"E0.sketch_text.stroke-214"),sQuery(id+"F0.wireOp",EDGE,"E0.sketch_text.stroke-215"),sQuery(id+"F0.wireOp",EDGE,"E0.sketch_text.stroke-216"),sQuery(id+"F0.wireOp",EDGE,"E0.sketch_text.stroke-217"),sQuery(id+"F0.wireOp",EDGE,"E0.sketch_text.stroke-218"),sQuery(id+"F0.wireOp",EDGE,"E0.sketch_text.stroke-219"),sQuery(id+"F0.wireOp",EDGE,"E0.sketch_text.stroke-220"),sQuery(id+"F0.wireOp",EDGE,"E0.sketch_text.stroke-221"),sQuery(id+"F0.wireOp",EDGE,"E0.sketch_text.stroke-222"),sQuery(id+"F0.wireOp",EDGE,"E0.sketch_text.stroke-223"),sQuery(id+"F0.wireOp",EDGE,"E0.sketch_text.stroke-224"),sQuery(id+"F0.wireOp",EDGE,"E0.sketch_text.stroke-225"),sQuery(id+"F0.wireOp",EDGE,"E0.sketch_text.stroke-226"),sQuery(id+"F0.wireOp",EDGE,"E0.sketch_text.stroke-227"),sQuery(id+"F0.wireOp",EDGE,"E0.sketch_text.stroke-228"),sQuery(id+"F0.wireOp",EDGE,"E0.sketch_text.stroke-229"),sQuery(id+"F0.wireOp",EDGE,"E0.sketch_text.stroke-230"),sQuery(id+"F0.wireOp",EDGE,"E0.sketch_text.stroke-241"),sQuery(id+"F0.wireOp",EDGE,"E0.sketch_text.stroke-242"),sQuery(id+"F0.wireOp",EDGE,"E0.sketch_text.stroke-243"),sQuery(id+"F0.wireOp",EDGE,"E0.sketch_text.stroke-244"),sQuery(id+"F0.wireOp",EDGE,"E0.sketch_text.stroke-245"),sQuery(id+"F0.wireOp",EDGE,"E0.sketch_text.stroke-246"),sQuery(id+"F0.wireOp",EDGE,"E0.sketch_text.stroke-247"),sQuery(id+"F0.wireOp",EDGE,"E0.sketch_text.stroke-248"),sQuery(id+"F0.wireOp",EDGE,"E0.sketch_text.stroke-249"),sQuery(id+"F0.wireOp",EDGE,"E0.sketch_text.stroke-250"),sQuery(id+"F0.wireOp",EDGE,"E0.sketch_text.stroke-251"),sQuery(id+"F0.wireOp",EDGE,"E0.sketch_text.stroke-252"),sQuery(id+"F0.wireOp",EDGE,"E0.sketch_text.stroke-253"),sQuery(id+"F0.wireOp",EDGE,"E0.sketch_text.stroke-254"),sQuery(id+"F0.wireOp",EDGE,"E0.sketch_text.stroke-255"),sQuery(id+"F0.wireOp",EDGE,"E0.sketch_text.stroke-256"),sQuery(id+"F0.wireOp",EDGE,"E0.sketch_text.stroke-257"),sQuery(id+"F0.wireOp",EDGE,"E0.sketch_text.stroke-258"),sQuery(id+"F0.wireOp",EDGE,"E0.sketch_text.stroke-259"),sQuery(id+"F0.wireOp",EDGE,"E0.sketch_text.stroke-260"),sQuery(id+"F0.wireOp",EDGE,"E0.sketch_text.stroke-261"),sQuery(id+"F0.wireOp",EDGE,"E0.sketch_text.stroke-262"),sQuery(id+"F0.wireOp",EDGE,"E0.sketch_text.stroke-263"),sQuery(id+"F0.wireOp",EDGE,"E0.sketch_text.stroke-264"),sQuery(id+"F0.wireOp",EDGE,"E0.sketch_text.stroke-265"),sQuery(id+"F0.wireOp",EDGE,"E0.sketch_text.stroke-266"),sQuery(id+"F0.wireOp",EDGE,"E0.sketch_text.stroke-267"),sQuery(id+"F0.wireOp",EDGE,"E0.sketch_text.stroke-268"),sQuery(id+"F0.wireOp",EDGE,"E0.sketch_text.stroke-269"),sQuery(id+"F0.wireOp",EDGE,"E0.sketch_text.stroke-270"),sQuery(id+"F0.wireOp",EDGE,"E0.sketch_text.stroke-271"),sQuery(id+"F0.wireOp",EDGE,"E0.sketch_text.stroke-272"),sQuery(id+"F0.wireOp",EDGE,"E0.sketch_text.stroke-273"),sQuery(id+"F0.wireOp",EDGE,"E0.sketch_text.stroke-274"),sQuery(id+"F0.wireOp",EDGE,"E0.sketch_text.stroke-275"),sQuery(id+"F0.wireOp",EDGE,"E0.sketch_text.stroke-276"),sQuery(id+"F0.wireOp",EDGE,"E0.sketch_text.stroke-277"),sQuery(id+"F0.wireOp",EDGE,"E0.sketch_text.stroke-278"),sQuery(id+"F0.wireOp",EDGE,"E0.sketch_text.stroke-279"),sQuery(id+"F0.wireOp",EDGE,"E0.sketch_text.stroke-280"),sQuery(id+"F0.wireOp",EDGE,"E0.sketch_text.stroke-281"),sQuery(id+"F0.wireOp",EDGE,"E0.sketch_text.stroke-282"),sQuery(id+"F0.wireOp",EDGE,"E0.sketch_text.stroke-283"),sQuery(id+"F0.wireOp",EDGE,"E0.sketch_text.stroke-284"),sQuery(id+"F0.wireOp",EDGE,"E0.sketch_text.stroke-285"),sQuery(id+"F0.wireOp",EDGE,"E0.sketch_text.stroke-286"),sQuery(id+"F0.wireOp",EDGE,"E0.sketch_text.stroke-287"),sQuery(id+"F0.wireOp",EDGE,"E0.sketch_text.stroke-288"),sQuery(id+"F0.wireOp",EDGE,"E0.sketch_text.stroke-289"),sQuery(id+"F0.wireOp",EDGE,"E0.sketch_text.stroke-290"),sQuery(id+"F0.wireOp",EDGE,"E0.sketch_text.stroke-291"),sQuery(id+"F0.wireOp",EDGE,"E0.sketch_text.stroke-292"),sQuery(id+"F0.wireOp",EDGE,"E0.sketch_text.stroke-293"),sQuery(id+"F0.wireOp",EDGE,"E0.sketch_text.stroke-294"),sQuery(id+"F0.wireOp",EDGE,"E0.sketch_text.stroke-295"),sQuery(id+"F0.wireOp",EDGE,"E0.sketch_text.stroke-296"),sQuery(id+"F0.wireOp",EDGE,"E0.sketch_text.stroke-297"),sQuery(id+"F0.wireOp",EDGE,"E0.sketch_text.stroke-298"),sQuery(id+"F0.wireOp",EDGE,"E0.sketch_text.stroke-299"),sQuery(id+"F0.wireOp",EDGE,"E0.sketch_text.stroke-300"),sQuery(id+"F0.wireOp",EDGE,"E0.sketch_text.stroke-301"),sQuery(id+"F0.wireOp",EDGE,"E0.sketch_text.stroke-302"),sQuery(id+"F0.wireOp",EDGE,"E0.sketch_text.stroke-303"),sQuery(id+"F0.wireOp",EDGE,"E0.sketch_text.stroke-304"),sQuery(id+"F0.wireOp",EDGE,"E0.sketch_text.stroke-305"),sQuery(id+"F0.wireOp",EDGE,"E0.sketch_text.stroke-306"),sQuery(id+"F0.wireOp",EDGE,"E0.sketch_text.stroke-307"),sQuery(id+"F0.wireOp",EDGE,"E0.sketch_text.stroke-308"),sQuery(id+"F0.wireOp",EDGE,"E0.sketch_text.stroke-309"),sQuery(id+"F0.wireOp",EDGE,"E0.sketch_text.stroke-310"),sQuery(id+"F0.wireOp",EDGE,"E0.sketch_text.stroke-311"),sQuery(id+"F0.wireOp",EDGE,"E0.sketch_text.stroke-312"),sQuery(id+"F0.wireOp",EDGE,"E0.sketch_text.stroke-313"),sQuery(id+"F0.wireOp",EDGE,"E0.sketch_text.stroke-314"),sQuery(id+"F0.wireOp",EDGE,"E0.sketch_text.stroke-315"),sQuery(id+"F0.wireOp",EDGE,"E0.sketch_text.stroke-316"),sQuery(id+"F0.wireOp",EDGE,"E0.sketch_text.stroke-317"),sQuery(id+"F0.wireOp",EDGE,"E0.sketch_text.stroke-318"),sQuery(id+"F0.wireOp",EDGE,"E0.sketch_text.stroke-319"),sQuery(id+"F0.wireOp",EDGE,"E0.sketch_text.stroke-320"),sQuery(id+"F0.wireOp",EDGE,"E0.sketch_text.stroke-321"),sQuery(id+"F0.wireOp",EDGE,"E0.sketch_text.stroke-322"),sQuery(id+"F0.wireOp",EDGE,"E0.sketch_text.stroke-323"),sQuery(id+"F0.wireOp",EDGE,"E0.sketch_text.stroke-324"),sQuery(id+"F0.wireOp",EDGE,"E0.sketch_text.stroke-325"),sQuery(id+"F0.wireOp",EDGE,"E0.sketch_text.stroke-326"),sQuery(id+"F0.wireOp",EDGE,"E0.sketch_text.stroke-327"),sQuery(id+"F0.wireOp",EDGE,"E0.sketch_text.stroke-328"),sQuery(id+"F0.wireOp",EDGE,"E0.sketch_text.stroke-329"),sQuery(id+"F0.wireOp",EDGE,"E0.sketch_text.stroke-330"),sQuery(id+"F0.wireOp",EDGE,"E0.sketch_text.stroke-331"),sQuery(id+"F0.wireOp",EDGE,"E0.sketch_text.stroke-332"),sQuery(id+"F0.wireOp",EDGE,"E0.sketch_text.stroke-333"),sQuery(id+"F0.wireOp",EDGE,"E0.sketch_text.stroke-334"),sQuery(id+"F0.wireOp",EDGE,"E0.sketch_text.stroke-335"),sQuery(id+"F0.wireOp",EDGE,"E0.sketch_text.stroke-336"),sQuery(id+"F0.wireOp",EDGE,"E0.sketch_text.stroke-337"),sQuery(id+"F0.wireOp",EDGE,"E0.sketch_text.stroke-338"),sQuery(id+"F0.wireOp",EDGE,"E0.sketch_text.stroke-339"),sQuery(id+"F0.wireOp",EDGE,"E0.sketch_text.stroke-348"),sQuery(id+"F0.wireOp",EDGE,"E0.sketch_text.stroke-349"),sQuery(id+"F0.wireOp",EDGE,"E0.sketch_text.stroke-350"),sQuery(id+"F0.wireOp",EDGE,"E0.sketch_text.stroke-351"),sQuery(id+"F0.wireOp",EDGE,"E0.sketch_text.stroke-352"),sQuery(id+"F0.wireOp",EDGE,"E0.sketch_text.stroke-353"),sQuery(id+"F0.wireOp",EDGE,"E0.sketch_text.stroke-354"),sQuery(id+"F0.wireOp",EDGE,"E0.sketch_text.stroke-355"),sQuery(id+"F0.wireOp",EDGE,"E0.sketch_text.stroke-356"),sQuery(id+"F0.wireOp",EDGE,"E0.sketch_text.stroke-357"),sQuery(id+"F0.wireOp",EDGE,"E0.sketch_text.stroke-358"),sQuery(id+"F0.wireOp",EDGE,"E0.sketch_text.stroke-359"),sQuery(id+"F0.wireOp",EDGE,"E0.sketch_text.stroke-360"),sQuery(id+"F0.wireOp",EDGE,"E0.sketch_text.stroke-361"),sQuery(id+"F0.wireOp",EDGE,"E0.sketch_text.stroke-362"),sQuery(id+"F0.wireOp",EDGE,"E0.sketch_text.stroke-363"),sQuery(id+"F0.wireOp",EDGE,"E0.sketch_text.stroke-364"),sQuery(id+"F0.wireOp",EDGE,"E0.sketch_text.stroke-365"),sQuery(id+"F0.wireOp",EDGE,"E0.sketch_text.stroke-366"),sQuery(id+"F0.wireOp",EDGE,"E0.sketch_text.stroke-367"),sQuery(id+"F0.wireOp",EDGE,"E0.sketch_text.stroke-368"),sQuery(id+"F0.wireOp",EDGE,"E0.sketch_text.stroke-369"),sQuery(id+"F0.wireOp",EDGE,"E0.sketch_text.stroke-370"),sQuery(id+"F0.wireOp",EDGE,"E0.sketch_text.stroke-371"),sQuery(id+"F0.wireOp",EDGE,"E0.sketch_text.stroke-372"),sQuery(id+"F0.wireOp",EDGE,"E0.sketch_text.stroke-373"),sQuery(id+"F0.wireOp",EDGE,"E0.sketch_text.stroke-374"),sQuery(id+"F0.wireOp",EDGE,"E1.bottom"),sQuery(id+"F0.wireOp",EDGE,"E1.top"),sQuery(id+"F0.wireOp",EDGE,"E2.filletArc"),sQuery(id+"F0.wireOp",EDGE,"E3.filletArc"),sQuery(id+"F0.wireOp",EDGE,"E5.filletArc"),sQuery(id+"F0.wireOp",EDGE,"E7"),sQuery(id+"F0.wireOp",EDGE,"E9"),sQuery(id+"F0.wireOp",EDGE,"E10.trimOffspring")])],"isStart":true});
            var Q2;
            Q2=makeQuery(id+"F0.imprint","IMPRINT",FACE,{"disambiguationData":[TD([[makeQuery(id+"F0.imprint","IMPRINT",EDGE,{"derivedFrom":sQuery(id+"F0.wireOp",EDGE,"E0.sketch_text.stroke-116")}),-1.0]])]});
            extrude(context, id + "F2", {"entities" : qUnion([Q0, Q1, Q2]), "depth" : 25 * mm, "offsetDistance" : 25 * mm});
        }
    });
